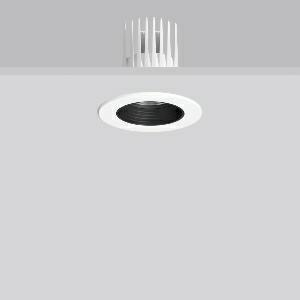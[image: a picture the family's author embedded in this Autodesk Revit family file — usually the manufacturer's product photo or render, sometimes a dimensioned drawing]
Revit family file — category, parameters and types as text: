
# Revit family: heledon_mini_e_901743_002_3_76_c07e
name_source: partatom
category: Lighting Fixtures
units: mm (PartAtom-declared; Revit-internal decimal feet)

## family parameters
Cut with Voids When Loaded = No
Host = Face
Light Source = No
Part Type = Normal
Room Calculation Point = No
Round Connector Dimension = Use Diameter
Shared = No

## types (1)
- HELEDON mini E (1 x LED Modul 935, 2250 lm, 3500)
    Apparent Load = 20 VA
    Approval mark = CE
    CIE Flux Codes = 99 100 100 100 100
    Color Rendering = 92
    Color Temperature = 3500
    Default Elevation = 1800 mm
    Description = Series: HELEDON mini
Round recessed downlight. Housing: die-cast aluminium, powder-coated. Black plastic ring and recessed LED to prevent glare from the side. Optical assembly with lens made of plastic (polycarbonate) for the best homogeneous light distribution - can be changed without tools. Best colour rendering index Ra>90. Suitable for Recessed ceiling mounting. Installation without tools thanks to spring fastening system. Including separate LED converter with connecting cable 600 mm.High quality converter without flickering and stroboscopic effect. Through-wiring box (5 pole) available as accessory. The following accessories can be mounted without use of tools: interchangeable lenses, decorative glasses, honeycomb louvre, clear and frosted diffusers, white interchangeable plastic ring. 
Colour: traffic white, matt (RAL 9016)
Diameter: 124 mm
Height: 3 mm
Cut-out diameter: 114 mm
Recess height: 170 mm
Luminaire: recess height: 120 mm
Lamp: LED
Socket: without socket
Colour temperature: 3500K
Colour rendering index (CRI): 92
System power: 20 W
Rated luminous flux: 2250 lm
Luminous efficiency: 113 lm/W
Control gear: Converter, dimmable, DALI
Protection class: II
Type of protection: IP 20
    Height = 0 mm  [stored 0 ft]
    Lamp = 1 x LED Modul 935
    Lamp Light Flux = 2250 lm
    Lamp count = 1
    Length = 124 mm  [stored 0.406824 ft]
    Lifetime = 50000 h
    Luminous efficacy = 113 lm/W
    Manufacturer = RZB
    ModVariant = No
    Model = 901743.002.3.76
    Mounting Place = Ceiling
    Mounting Type = Recessed
    Number of Poles = 1
    OnlyDefault = Yes
    Power Factor = 1
    Product Name = HELEDON mini E
    Product group = Recessed downlights
    ProductGroupID = 402
    Protection Class = Protection class II
    Protection Degree = IP 20
    RLX_Detail_Level = 1
    RLX_Emergency_Light_Flux = 0 lm
    RLX_Emergency_Type = 0
    RLX_Emergency_Type_DB = No
    RlxData = <blob elided: 127165 chars, md5=bfabb7d0>
    Socket = socket
    Standby Power = 0 W
    System Light Flux = 2250 lm
    System Power = 20 W
    Type Comments = Product without accessories
    Type Image = 901656.002.jpg
    URL = http://relux.com
    VarID = ---
    Voltage = 230 V
    Voltage Range = 220-240 V
    Weight = 0.00 kg
    Width = 0 mm  [stored 0 ft]

note: [stored X ft] marks values corroborated as IEEE doubles in the binary element streams (Revit-internal decimal feet)

## geometry (parser evidence)
native form markers: Blend x4, Sweep x12
no freeform markers — native parametric forms only
